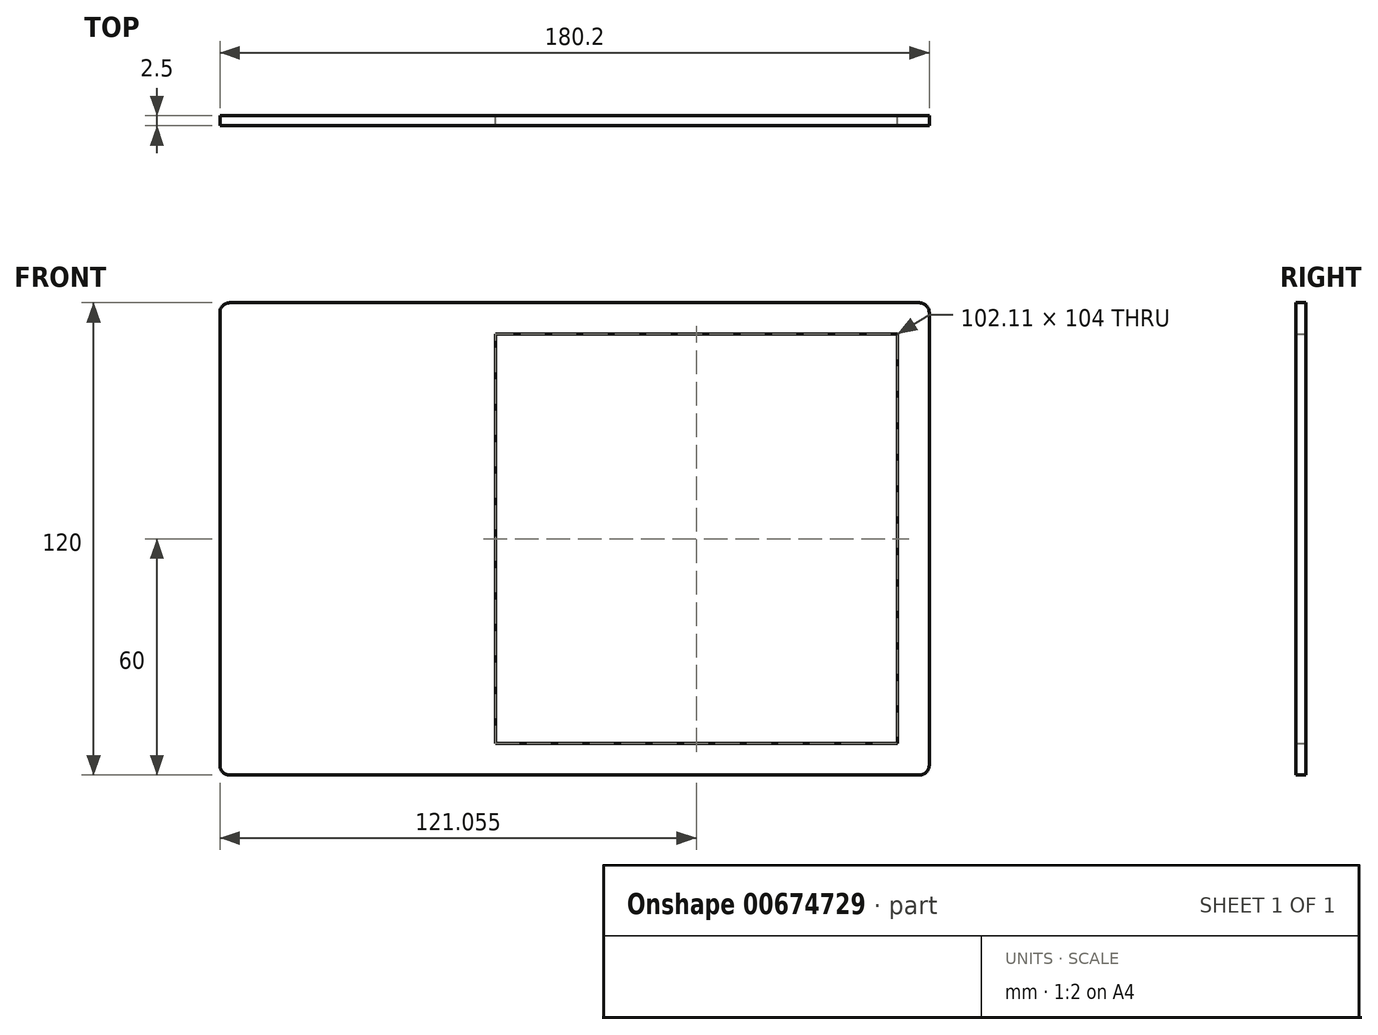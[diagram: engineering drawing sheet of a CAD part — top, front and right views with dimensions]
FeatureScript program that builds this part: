
annotation { "Feature Type Name" : "Feature", "Feature Type Description" : "" }
export const myFeature = defineFeature(function(context is Context, id is Id, definition is map)
    precondition{}
    {
        {
            var Q0;
            Q0=qCreatedBy(makeId("Front.planeOp"),FACE);
            var sketch = newSketch(context, id + "F0", { "sketchPlane" : qUnion([Q0])});
            skLineSegment(sketch, "E0.bottom", {"start": v(-90.1, 60) * mm, "end": v(90.1, 60) * mm});
            skLineSegment(sketch, "E0.top", {"start": v(-90.1, -60) * mm, "end": v(90.1, -60) * mm});
            skLineSegment(sketch, "E0.left", {"start": v(-90.1, 60) * mm, "end": v(-90.1, -60) * mm});
            skLineSegment(sketch, "E0.right", {"start": v(90.1, 60) * mm, "end": v(90.1, -60) * mm});
            skPoint(sketch, "E0.middle", {"position": v(0, 0) * mm});
            skLineSegment(sketch, "E1", {"start": v(-20.1, 60) * mm, "end": v(-20.1, -60) * mm});
            skLineSegment(sketch, "E2", {"start": v(-20.1, 52) * mm, "end": v(90.1, 52) * mm});
            skLineSegment(sketch, "E3", {"start": v(90.1, 52) * mm, "end": v(82.01, 52) * mm});
            skLineSegment(sketch, "E4", {"start": v(82.01, 52) * mm, "end": v(82.01, -60) * mm});
            skLineSegment(sketch, "E5", {"start": v(-20.1, -52) * mm, "end": v(82.01, -52) * mm});
            skLineSegment(sketch, "E6", {"start": v(82.01, -60) * mm, "end": v(90.1, -60) * mm});
            skLineSegment(sketch, "E7", {"start": v(-20.1, 60) * mm, "end": v(-20.1, 52) * mm});
            skSolve(sketch);
        }
        {
            var Q0;
            {var subQ0=sQuery(id+"F0.wireOp",EDGE,"E0.left");Q0=makeQuery(id+"F0.imprint","IMPRINT",FACE,{"disambiguationData":[TD([[makeQuery(id+"F0.imprint","IMPRINT",EDGE,{"derivedFrom":subQ0}),1.0]])]});}
            extrude(context, id + "F1", {"entities" : qUnion([Q0]), "depth" : 2.5 * mm, "offsetDistance" : 25 * mm});
        }
        {
            var Q0;
            {var subQ1=sQuery(id+"F0.wireOp",EDGE,"E1");var subQ4=sQuery(id+"F0.wireOp",EDGE,"E0.bottom");var subQ5=makeQuery(id+"F0.imprint","INTERSECT",VERTEX,{"derivedFrom":[subQ4,subQ1]});Q0=makeQuery(id+"F0.imprint","IMPRINT",FACE,{"disambiguationData":[TD([[makeQuery(id+"F0.imprint","IMPRINT",EDGE,{"disambiguationData":[TD([[subQ5,-1.0]])],"derivedFrom":subQ4}),-1.0]])]});}
            extrude(context, id + "F2", {"entities" : qUnion([Q0]), "operationType" : NewBodyOperationType.ADD, "depth" : 2.5 * mm, "offsetDistance" : 25 * mm});
        }
        {
            var Q0;
            {var subQ4=sQuery(id+"F0.wireOp",EDGE,"E0.right");var subQ6=sQuery(id+"F0.wireOp",EDGE,"E0.top");var subQ7=makeQuery(id+"F0.imprint","INTERSECT",VERTEX,{"derivedFrom":[subQ6,subQ4]});Q0=makeQuery(id+"F0.imprint","IMPRINT",FACE,{"disambiguationData":[TD([[makeQuery(id+"F0.imprint","IMPRINT",EDGE,{"disambiguationData":[TD([[subQ7,1.0]])],"derivedFrom":subQ6}),1.0]])]});}
            extrude(context, id + "F3", {"entities" : qUnion([Q0]), "operationType" : NewBodyOperationType.ADD, "depth" : 2.5 * mm, "offsetDistance" : 25 * mm});
        }
        {
            var Q0;
            {var subQ5=sQuery(id+"F0.wireOp",EDGE,"E5");Q0=makeQuery(id+"F0.imprint","IMPRINT",FACE,{"disambiguationData":[TD([[makeQuery(id+"F0.imprint","IMPRINT",EDGE,{"derivedFrom":subQ5}),-1.0]])]});}
            extrude(context, id + "F4", {"entities" : qUnion([Q0]), "operationType" : NewBodyOperationType.ADD, "depth" : 2.5 * mm, "offsetDistance" : 25 * mm});
        }
        {
            var Q0;
            {var subQ4=sQuery(id+"F0.wireOp",EDGE,"E0.right");var subQ6=sQuery(id+"F0.wireOp",EDGE,"E0.top");var subQ7=makeQuery(id+"F0.imprint","INTERSECT",VERTEX,{"derivedFrom":[subQ6,subQ4]});Q0=makeQuery(id+"F0.imprint","IMPRINT",FACE,{"disambiguationData":[TD([[makeQuery(id+"F0.imprint","IMPRINT",EDGE,{"disambiguationData":[TD([[subQ7,1.0]])],"derivedFrom":subQ6}),1.0]])]});}
            extrude(context, id + "F5", {"entities" : qUnion([Q0]), "operationType" : NewBodyOperationType.ADD, "depth" : 2.5 * mm, "offsetDistance" : 25 * mm});
        }
        {
            var Q0;
            Q0=makeQuery(id+"F1.opExtrude","SWEPT_EDGE",EDGE,{"disambiguationData":[OSD([sQuery(id+"F0.wireOp",EDGE,"E0.bottom"),sQuery(id+"F0.wireOp",EDGE,"E0.left")])]});
            fillet(context, id + "F6", {"entities" : qUnion([Q0]), "radius" : 2.5 * mm, "tangentPropagation" : true, "allowEdgeOverflow" : false});
        }
        {
            var Q0;
            Q0=makeQuery(id+"F2.opExtrude","SWEPT_EDGE",EDGE,{"disambiguationData":[OSD([sQuery(id+"F0.wireOp",EDGE,"E0.bottom"),sQuery(id+"F0.wireOp",EDGE,"E0.right")])]});
            fillet(context, id + "F7", {"entities" : qUnion([Q0]), "radius" : 2.5 * mm, "tangentPropagation" : true, "allowEdgeOverflow" : false});
        }
        {
            var Q0;
            Q0=makeQuery(id+"F3.opExtrude","SWEPT_EDGE",EDGE,{"disambiguationData":[OSD([sQuery(id+"F0.wireOp",EDGE,"E0.top"),sQuery(id+"F0.wireOp",EDGE,"E0.right")])]});
            fillet(context, id + "F8", {"entities" : qUnion([Q0]), "radius" : 2.5 * mm, "tangentPropagation" : true, "allowEdgeOverflow" : false});
        }
        {
            var Q0;
            Q0=makeQuery(id+"F1.opExtrude","SWEPT_EDGE",EDGE,{"disambiguationData":[OSD([sQuery(id+"F0.wireOp",EDGE,"E0.top"),sQuery(id+"F0.wireOp",EDGE,"E0.left")])]});
            fillet(context, id + "F9", {"entities" : qUnion([Q0]), "radius" : 2.5 * mm, "tangentPropagation" : true, "allowEdgeOverflow" : false});
        }
    });
